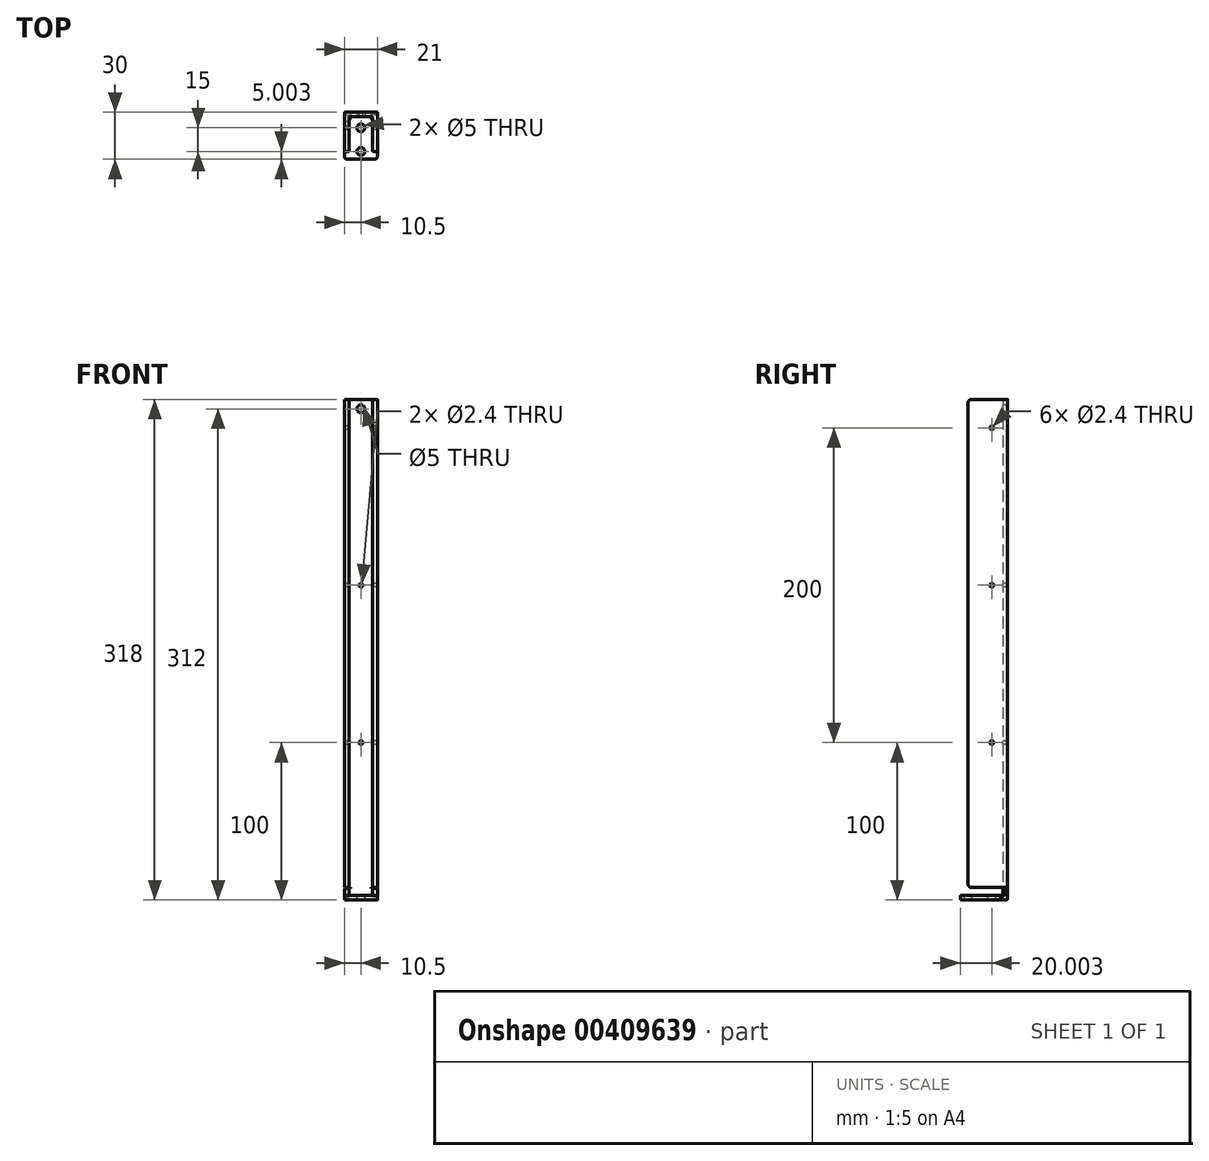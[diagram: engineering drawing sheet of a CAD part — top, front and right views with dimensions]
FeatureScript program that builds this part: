
annotation { "Feature Type Name" : "Feature", "Feature Type Description" : "" }
export const myFeature = defineFeature(function(context is Context, id is Id, definition is map)
    precondition{}
    {
        {
            var Q0;
            Q0=qCreatedBy(makeId("Right.planeOp"),FACE);
            var sketch = newSketch(context, id + "F0", { "sketchPlane" : qUnion([Q0])});
            skLineSegment(sketch, "E0", {"start": v(-7.6, 0) * mm, "end": v(22.4, 0) * mm});
            skLineSegment(sketch, "E1", {"start": v(22.4, 0) * mm, "end": v(22.4, 318) * mm});
            skLineSegment(sketch, "E2", {"start": v(22.4, 318) * mm, "end": v(19.4, 318) * mm});
            skLineSegment(sketch, "E3", {"start": v(19.4, 318) * mm, "end": v(19.4, 3) * mm});
            skLineSegment(sketch, "E4", {"start": v(19.4, 3) * mm, "end": v(-7.6, 3) * mm});
            skLineSegment(sketch, "E5", {"start": v(-7.6, 3) * mm, "end": v(-7.6, 0) * mm});
            skSolve(sketch);
        }
        {
            var Q0;
            Q0 = qSketchRegion(id + "F0", true);
            extrude(context, id + "F1", {"entities" : qUnion([Q0]), "depth" : 15 * mm});
        }
        {
            var Q0;
            Q0=makeQuery(id+"F1.opExtrude","SWEPT_FACE",FACE,{"disambiguationData":[OSD([sQuery(id+"F0.wireOp",EDGE,"E1")])]});
            var sketch = newSketch(context, id + "F2", { "sketchPlane" : qUnion([Q0])});
            skLineSegment(sketch, "E6.bottom", {"start": v(0, 8) * mm, "end": v(3, 8) * mm});
            skLineSegment(sketch, "E6.top", {"start": v(0, 318) * mm, "end": v(3, 318) * mm});
            skLineSegment(sketch, "E6.left", {"start": v(0, 8) * mm, "end": v(0, 318) * mm});
            skLineSegment(sketch, "E6.right", {"start": v(3, 8) * mm, "end": v(3, 318) * mm});
            skLineSegment(sketch, "E7.bottom", {"start": v(-15, 318) * mm, "end": v(-18, 318) * mm});
            skLineSegment(sketch, "E7.top", {"start": v(-15, 8) * mm, "end": v(-18, 8) * mm});
            skLineSegment(sketch, "E7.left", {"start": v(-15, 318) * mm, "end": v(-15, 8) * mm});
            skLineSegment(sketch, "E7.right", {"start": v(-18, 318) * mm, "end": v(-18, 8) * mm});
            skSolve(sketch);
        }
        {
            var Q0;
            Q0 = qSketchRegion(id + "F2", true);
            extrude(context, id + "F3", {"entities" : qUnion([Q0]), "operationType" : NewBodyOperationType.ADD, "oppositeDirection" : true, "depth" : 25 * mm});
        }
        {
            var Q0;
            Q0=makeQuery(id+"F1.opExtrude","SWEPT_FACE",FACE,{"disambiguationData":[OSD([sQuery(id+"F0.wireOp",EDGE,"E4")])]});
            var sketch = newSketch(context, id + "F4", { "sketchPlane" : qUnion([Q0])});
            skCircle(sketch, "E8", {"center": v(7.5, -2.6) * mm, "radius": 2.5 * mm});
            skCircle(sketch, "E9", {"center": v(7.5, 12.4) * mm, "radius": 2.5 * mm});
            skCircle(sketch, "E10", {"center": v(7.5, 12.4) * mm, "radius": 4.5 * mm, "construction": true});
            skCircle(sketch, "E11", {"center": v(7.5, -2.6) * mm, "radius": 4.46 * mm, "construction": true});
            skSolve(sketch);
        }
        {
            var Q0;
            Q0 = qSketchRegion(id + "F4", true);
            extrude(context, id + "F5", {"entities" : qUnion([Q0]), "operationType" : NewBodyOperationType.REMOVE, "oppositeDirection" : true, "depth" : 3 * mm});
        }
        {
            var Q0;
            Q0=makeQuery(id+"F1.opExtrude","SWEPT_FACE",FACE,{"disambiguationData":[OSD([sQuery(id+"F0.wireOp",EDGE,"E3")])]});
            var sketch = newSketch(context, id + "F6", { "sketchPlane" : qUnion([Q0])});
            skLineSegment(sketch, "E12.bottom", {"start": v(0, 8) * mm, "end": v(1, 8) * mm});
            skLineSegment(sketch, "E12.top", {"start": v(0, 7.5) * mm, "end": v(1, 7.5) * mm});
            skLineSegment(sketch, "E12.left", {"start": v(0, 8) * mm, "end": v(0, 7.5) * mm});
            skLineSegment(sketch, "E12.right", {"start": v(1, 8) * mm, "end": v(1, 7.5) * mm});
            skLineSegment(sketch, "E13.bottom", {"start": v(15, 8) * mm, "end": v(14, 8) * mm});
            skLineSegment(sketch, "E13.top", {"start": v(15, 7.5) * mm, "end": v(14, 7.5) * mm});
            skLineSegment(sketch, "E13.left", {"start": v(15, 8) * mm, "end": v(15, 7.5) * mm});
            skLineSegment(sketch, "E13.right", {"start": v(14, 8) * mm, "end": v(14, 7.5) * mm});
            skSolve(sketch);
        }
        {
            var Q0;
            Q0 = qSketchRegion(id + "F6", true);
            extrude(context, id + "F7", {"entities" : qUnion([Q0]), "operationType" : NewBodyOperationType.REMOVE, "oppositeDirection" : true, "depth" : 3 * mm});
        }
        {
            var Q0;
            Q0=makeQuery(id+"F1.opExtrude","SWEPT_EDGE",EDGE,{"disambiguationData":[OSD([sQuery(id+"F0.wireOp",EDGE,"E3"),sQuery(id+"F0.wireOp",EDGE,"E4")])]});
            var Q1;
            Q1=makeQuery(id+"F1.opExtrude","SWEPT_EDGE",EDGE,{"disambiguationData":[OSD([sQuery(id+"F0.wireOp",EDGE,"E0"),sQuery(id+"F0.wireOp",EDGE,"E1")])]});
            var Q2;
            {var subQ0=sQuery(id+"F0.wireOp",EDGE,"E3");Q2=makeQuery(id+"F3.boolean.opBoolean","SPLIT",EDGE,{"disambiguationData":[topologyDisambiguationEdgeConnected([makeQuery(id+"F3.opExtrude","SWEPT_FACE",FACE,{"disambiguationData":[OSD([sQuery(id+"F2.wireOp",EDGE,"E6.left")])]})])],"derivedFrom":makeQuery(id+"F1.opExtrude","CAP_EDGE",EDGE,{"disambiguationData":[OSD([subQ0])],"isStart":true})});}
            var Q3;
            Q3=makeQuery(id+"F3.opExtrude","CAP_EDGE",EDGE,{"disambiguationData":[OSD([sQuery(id+"F2.wireOp",EDGE,"E6.right")])],"isStart":true});
            var Q4;
            Q4=makeQuery(id+"F3.opExtrude","CAP_EDGE",EDGE,{"disambiguationData":[OSD([sQuery(id+"F2.wireOp",EDGE,"E7.right")])],"isStart":true});
            var Q5;
            {var subQ0=sQuery(id+"F0.wireOp",EDGE,"E3");Q5=makeQuery(id+"F3.boolean.opBoolean","SPLIT",EDGE,{"disambiguationData":[topologyDisambiguationEdgeConnected([makeQuery(id+"F3.opExtrude","SWEPT_FACE",FACE,{"disambiguationData":[OSD([sQuery(id+"F2.wireOp",EDGE,"E7.left")])]})])],"derivedFrom":makeQuery(id+"F1.opExtrude","CAP_EDGE",EDGE,{"disambiguationData":[OSD([subQ0])],"isStart":false})});}
            var Q6;
            Q6=makeQuery(id+"FqQp6dOOzKqRe4i_1.boolean.opBoolean","COPY",EDGE,{"derivedFrom":makeQuery(id+"FqQp6dOOzKqRe4i_1.opExtrude","CAP_EDGE",EDGE,{"disambiguationData":[OSD([sQuery(id+"FuQxhJIuyBZaYl9_1.wireOp",EDGE,"ZrIXolOl-gWOG-G3Ii-Wei4-7PRN7w7ykNvu.left")])],"isStart":false})});
            var Q7;
            Q7=makeQuery(id+"FqQp6dOOzKqRe4i_1.boolean.opBoolean","COPY",EDGE,{"derivedFrom":makeQuery(id+"FqQp6dOOzKqRe4i_1.opExtrude","CAP_EDGE",EDGE,{"disambiguationData":[OSD([sQuery(id+"FuQxhJIuyBZaYl9_1.wireOp",EDGE,"ZrIXolOl-gWOG-G3Ii-Wei4-7PRN7w7ykNvu.right")])],"isStart":false})});
            fillet(context, id + "F8", {"entities" : qUnion([Q0, Q1, Q2, Q3, Q4, Q5, Q6, Q7]), "radius" : 1 * mm, "tangentPropagation" : true, "allowEdgeOverflow" : false});
        }
        {
            var Q0;
            Q0=makeQuery(id+"F1.opExtrude","SWEPT_FACE",FACE,{"disambiguationData":[OSD([sQuery(id+"F0.wireOp",EDGE,"E3")])]});
            var sketch = newSketch(context, id + "F9", { "sketchPlane" : qUnion([Q0])});
            skCircle(sketch, "E14", {"center": v(7.5, 312) * mm, "radius": 2.5 * mm});
            skPoint(sketch, "E14.centerSnap0", {"position": v(7.5, 318) * mm});
            skCircle(sketch, "E15", {"center": v(7.5, 100) * mm, "radius": 1.2 * mm});
            skPoint(sketch, "E15.centerSnap0", {"position": v(7.5, 4) * mm});
            skCircle(sketch, "E16", {"center": v(7.5, 200) * mm, "radius": 1.2 * mm});
            skSolve(sketch);
        }
        {
            var Q0;
            Q0 = qSketchRegion(id + "F9", true);
            extrude(context, id + "F10", {"entities" : qUnion([Q0]), "operationType" : NewBodyOperationType.REMOVE, "oppositeDirection" : true, "depth" : 3 * mm});
        }
        {
            var Q0;
            Q0=makeQuery(id+"F3.opExtrude","SWEPT_FACE",FACE,{"disambiguationData":[OSD([sQuery(id+"F2.wireOp",EDGE,"E6.right")])]});
            var sketch = newSketch(context, id + "F11", { "sketchPlane" : qUnion([Q0])});
            skCircle(sketch, "E17", {"center": v(-12.4, 300) * mm, "radius": 1.2 * mm});
            skCircle(sketch, "E18", {"center": v(-12.4, 100) * mm, "radius": 1.2 * mm});
            skLineSegment(sketch, "E19", {"start": v(-14.4, 98) * mm, "end": v(-14.4, -49.26) * mm, "construction": true});
            skLineSegment(sketch, "E20", {"start": v(103.6, 103.79) * mm, "end": v(103.6, -31.5) * mm, "construction": true});
            skLineSegment(sketch, "E21", {"start": v(-16.4, 98.96) * mm, "end": v(-16.4, 90.53) * mm, "construction": true});
            skLineSegment(sketch, "E22", {"start": v(105.6, 89.13) * mm, "end": v(105.6, 82.47) * mm, "construction": true});
            skCircle(sketch, "E23", {"center": v(-12.4, 200) * mm, "radius": 1.2 * mm});
            skSolve(sketch);
        }
        {
            var Q0;
            Q0 = qSketchRegion(id + "F11", true);
            extrude(context, id + "F12", {"entities" : qUnion([Q0]), "operationType" : NewBodyOperationType.REMOVE, "oppositeDirection" : true, "depth" : 34.2 * mm});
        }
        {
            var Q0;
            Q0=makeQuery(id+"F1.opExtrude","CAP_FACE",FACE,{"disambiguationData":[OSD([sQuery(id+"F0.wireOp",EDGE,"E0"),sQuery(id+"F0.wireOp",EDGE,"E1"),sQuery(id+"F0.wireOp",EDGE,"E2"),sQuery(id+"F0.wireOp",EDGE,"E3"),sQuery(id+"F0.wireOp",EDGE,"E4"),sQuery(id+"F0.wireOp",EDGE,"E5")])],"isStart":true});
            extrude(context, id + "F13", {"entities" : qUnion([Q0]), "operationType" : NewBodyOperationType.ADD, "depth" : 3 * mm});
        }
        {
            var Q0;
            Q0=makeQuery(id+"F1.opExtrude","CAP_FACE",FACE,{"disambiguationData":[OSD([sQuery(id+"F0.wireOp",EDGE,"E0"),sQuery(id+"F0.wireOp",EDGE,"E1"),sQuery(id+"F0.wireOp",EDGE,"E2"),sQuery(id+"F0.wireOp",EDGE,"E3"),sQuery(id+"F0.wireOp",EDGE,"E4"),sQuery(id+"F0.wireOp",EDGE,"E5")])],"isStart":false});
            extrude(context, id + "F14", {"entities" : qUnion([Q0]), "operationType" : NewBodyOperationType.ADD, "depth" : 3 * mm});
        }
        {
            var Q0;
            Q0=makeQuery(id+"F3.opExtrude","CAP_EDGE",EDGE,{"disambiguationData":[OSD([sQuery(id+"F2.wireOp",EDGE,"E6.bottom")])],"isStart":false});
            var Q1;
            Q1=makeQuery(id+"F3.opExtrude","CAP_EDGE",EDGE,{"disambiguationData":[OSD([sQuery(id+"F2.wireOp",EDGE,"E7.top")])],"isStart":false});
            var Q2;
            Q2=makeQuery(id+"F13.opExtrude","CAP_EDGE",EDGE,{"disambiguationData":[OSD([sQuery(id+"F0.wireOp",EDGE,"E5")])],"isStart":false});
            var Q3;
            Q3=makeQuery(id+"F14.opExtrude","CAP_EDGE",EDGE,{"disambiguationData":[OSD([sQuery(id+"F0.wireOp",EDGE,"E5")])],"isStart":false});
            var Q4;
            Q4=makeQuery(id+"F3.opExtrude","CAP_EDGE",EDGE,{"disambiguationData":[OSD([sQuery(id+"F2.wireOp",EDGE,"E6.top")])],"isStart":false});
            var Q5;
            Q5=makeQuery(id+"F3.opExtrude","CAP_EDGE",EDGE,{"disambiguationData":[OSD([sQuery(id+"F2.wireOp",EDGE,"E7.bottom")])],"isStart":false});
            fillet(context, id + "F15", {"entities" : qUnion([Q0, Q1, Q2, Q3, Q4, Q5]), "radius" : 2 * mm, "tangentPropagation" : true, "allowEdgeOverflow" : false});
        }
    });
